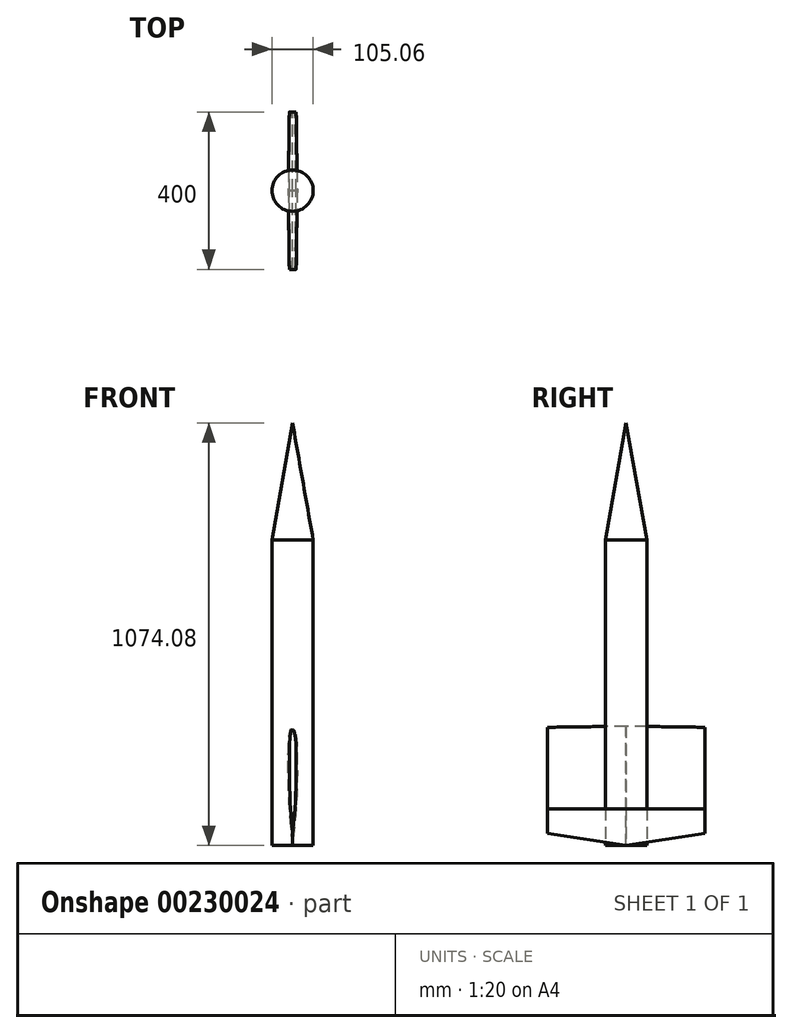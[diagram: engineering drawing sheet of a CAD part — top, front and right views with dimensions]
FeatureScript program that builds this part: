
annotation { "Feature Type Name" : "Feature", "Feature Type Description" : "" }
export const myFeature = defineFeature(function(context is Context, id is Id, definition is map)
    precondition{}
    {
        {
            var Q0;
            Q0=qCreatedBy(makeId("Top.planeOp"),FACE);
            var sketch = newSketch(context, id + "F1", { "sketchPlane" : qUnion([Q0])});
            skCircle(sketch, "E0", {"center": v(0, 0) * mm, "radius": 52.53 * mm});
            skSolve(sketch);
        }
        {
            var Q0;
            Q0 = qSketchRegion(id + "F1", true);
            extrude(context, id + "F0", {"entities" : qUnion([Q0]), "depth" : 776.15 * mm});
        }
        {
            var Q0;
            Q0=makeQuery(id+"F0.opExtrude","CAP_FACE",FACE,{"disambiguationData":[OSD([sQuery(id+"F1.wireOp",EDGE,"E0")])],"isStart":false});
            var sketch = newSketch(context, id + "F2", { "sketchPlane" : qUnion([Q0])});
            skSolve(sketch);
        }
        {
            var Q0;
            Q0=makeQuery(id+"F2.imprint","IMPRINT",FACE,{"disambiguationData":[TD([[makeQuery(id+"F2.imprint","IMPRINT",EDGE,{"derivedFrom":makeQuery(id+"F0.opExtrude","CAP_EDGE",EDGE,{"disambiguationData":[OSD([sQuery(id+"F1.wireOp",EDGE,"E0")])],"isStart":false})}),1.0]])]});
            extrude(context, id + "F3", {"entities" : qUnion([Q0]), "depth" : 3000 * mm, "hasDraft" : true, "draftAngle" : 10 * degree, "draftPullDirection" : true});
        }
        {
            var Q0;
            Q0=qCreatedBy(makeId("Front.planeOp"),FACE);
            var sketch = newSketch(context, id + "F4", { "sketchPlane" : qUnion([Q0])});
            skLineSegment(sketch, "E1", {"start": v(0, 0) * mm, "end": v(-8.23, 92.9) * mm});
            skLineSegment(sketch, "E2", {"start": v(-8.23, 92.9) * mm, "end": v(0, 0) * mm});
            skLineSegment(sketch, "E3", {"start": v(8.87, 93.54) * mm, "end": v(0, 0) * mm});
            skFitSpline(sketch, "E4", {"points": [v(-8.23, 92.9) * mm, v(-8.23, 283.4) * mm, v(0, 303.45) * mm, v(8.83, 282.1) * mm, v(8.87, 93.54) * mm], "startDerivative": vector(-8.58, 116.43) * mm, "endDerivative": vector(-16.15, -112.6) * mm});
            skSolve(sketch);
        }
        {
            var Q0;
            Q0 = qSketchRegion(id + "F4", true);
            extrude(context, id + "F5", {"entities" : qUnion([Q0]), "depth" : 200 * mm, "hasDraft" : true, "draftAngle" : 0.8 * degree, "draftPullDirection" : true, "hasSecondDirection" : true, "secondDirectionOppositeDirection" : true, "secondDirectionDepth" : 200 * mm, "hasSecondDirectionDraft" : true, "secondDirectionDraftAngle" : 0.8 * degree, "secondDirectionDraftPullDirection" : true});
        }
    });
